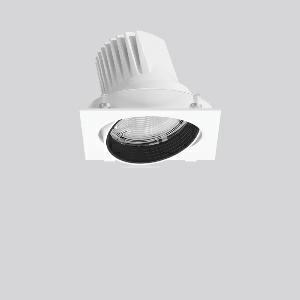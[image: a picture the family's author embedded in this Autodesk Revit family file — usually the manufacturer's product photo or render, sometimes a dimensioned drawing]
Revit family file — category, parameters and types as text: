
# Revit family: magcardo_maxi_722205_002_5cc5
name_source: partatom
category: Lighting Fixtures
units: mm (PartAtom-declared; Revit-internal decimal feet)

## family parameters
Cut with Voids When Loaded = No
Host = Face
Light Source = No
Part Type = Normal
Room Calculation Point = No
Round Connector Dimension = Use Diameter
Shared = No

## types (1)
- MAGCARDO maxi (1 x LED Modul 932 fresh meat, 1750 lm, 3200)
    Apparent Load = 33 VA
    Approval mark = CE
    CIE Flux Codes = 96 99 100 100 100
    Color Rendering = 90
    Color Temperature = 3200
    Default Elevation = 1800 mm
    Description = Series: MAGCARDO maxi
Projector unit for tool-free mounting in separate recessed frame. Luminaire top: die-cast aluminium, powder-coated. Rotation range 356° and swivel range ± 35°. Inner cover prevents view into the false ceiling. Black plastic ring and recessed LED to prevent glare from the side. Optical assembly with lens made of plastic (polycarbonate) for the best homogeneous light distribution - can be changed without tools. Special LED for illumination of meat included. Magnetic click locking mechanism for quick and convenient installation without tools: insert the recessed frame (1, 2 or 3-lamp) with clamp fastener (no tools required), push the luminaire head with the base plate into the recessed frame and fix magnetically. Including separate LED converter with connecting cable 600 mm.High quality converter without flickering and stroboscopic effect. Through-wiring box (5 pole) available as accessory. The following accessories can be mounted without use of tools: interchangeable lenses, honeycomb louvre, clear and frosted diffusers, white interchangeable plastic ring.Modular design: recessed mounting frame must be ordered separately! 
Colour: traffic white, matt (RAL 9016)
Length: 172 mm
Width: 167 mm
Height: 137 mm
Recess height: 155 mm
Lamp: LED
Socket: without socket
Colour temperature: fresh meat
System power: 33 W
Rated luminous flux: 1750 lm
Luminous efficiency: 53 lm/W
Control gear: Regulated power supply
Protection class: II
Type of protection: IP 20
    Height = 0 mm  [stored 0 ft]
    Lamp = 1 x LED Modul 932 fresh meat
    Lamp Light Flux = 1750 lm
    Lamp count = 1
    Length = 172 mm
    Lifetime = 50000 h
    Luminous efficacy = 53 lm/W
    Manufacturer = RZB
    ModVariant = No
    Model = 722205.002
    Mounting Place = Ceiling, Wall
    Mounting Type = Recessed
    Number of Poles = 1
    OnlyDefault = Yes
    Power Factor = 1
    Product Name = MAGCARDO maxi
    Product group = Recessed projectors
    ProductGroupID = 401
    Protection Class = Protection class II
    Protection Degree = IP 20
    RLX_Detail_Level = 1
    RLX_Emergency_Light_Flux = 0 lm
    RLX_Emergency_Type = 0
    RLX_Emergency_Type_DB = No
    RlxData = <blob elided: 40077 chars, md5=49d94c7d>
    Socket = socket
    Standby Power = 0 W
    System Light Flux = 1750 lm
    System Power = 33 W
    Type Comments = Product without accessories
    Type Image = 722048.002.jpg
    URL = http://relux.com
    VarID = ---
    Voltage = 230 V
    Voltage Range = 220-240 V
    Weight = 0.00 kg
    Width = 167 mm

note: [stored X ft] marks values corroborated as IEEE doubles in the binary element streams (Revit-internal decimal feet)

## geometry (parser evidence)
native form markers: Blend x4, Sweep x13
no freeform markers — native parametric forms only
